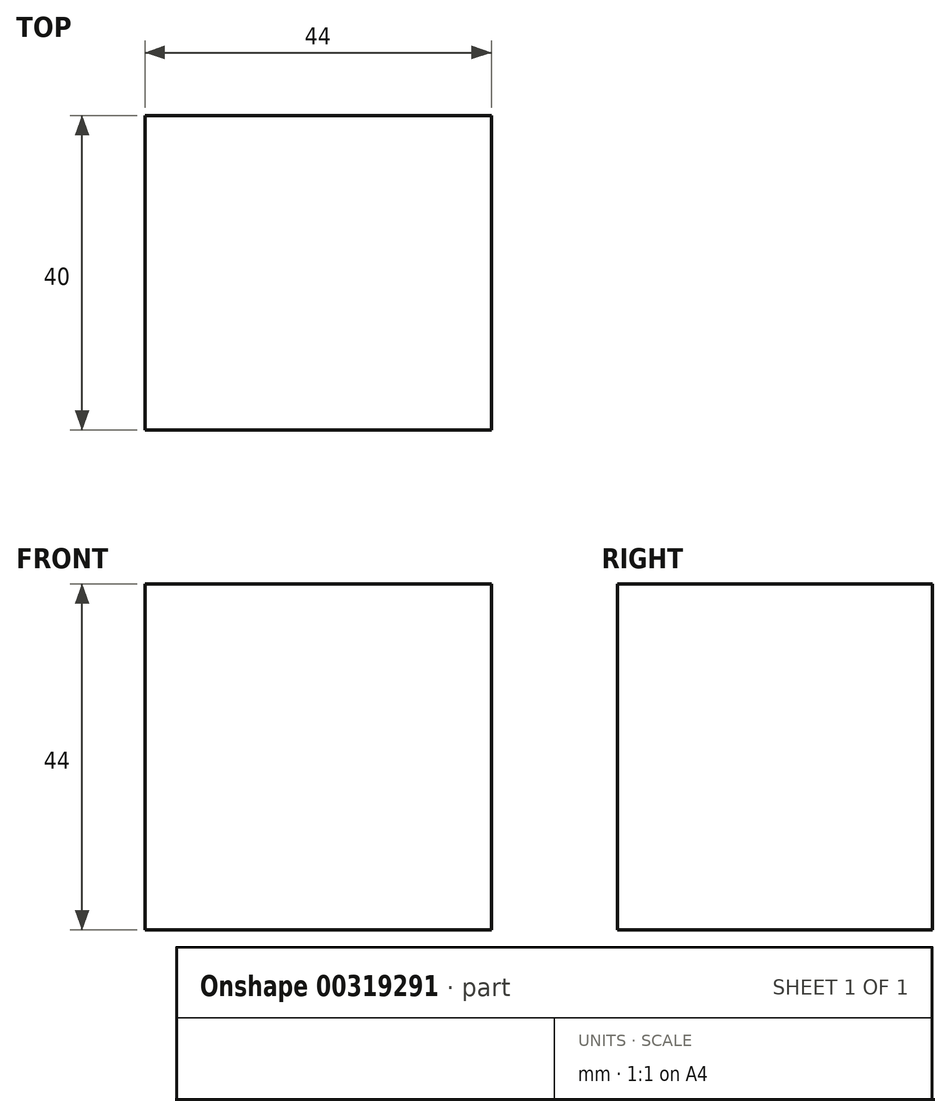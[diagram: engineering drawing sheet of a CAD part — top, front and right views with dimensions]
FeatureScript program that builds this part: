
annotation { "Feature Type Name" : "Feature", "Feature Type Description" : "" }
export const myFeature = defineFeature(function(context is Context, id is Id, definition is map)
    precondition{}
    {
        {
            var Q0;
            Q0=qCreatedBy(makeId("Front.planeOp"),FACE);
            var sketch = newSketch(context, id + "F0", { "sketchPlane" : qUnion([Q0])});
            skLineSegment(sketch, "E0.bottom", {"start": v(0, 0) * mm, "end": v(44, 0) * mm});
            skLineSegment(sketch, "E0.top", {"start": v(0, 44) * mm, "end": v(44, 44) * mm});
            skLineSegment(sketch, "E0.left", {"start": v(0, 0) * mm, "end": v(0, 44) * mm});
            skLineSegment(sketch, "E0.right", {"start": v(44, 0) * mm, "end": v(44, 44) * mm});
            skSolve(sketch);
        }
        {
            var Q0;
            Q0=makeQuery(id+"F0.imprint","IMPRINT",FACE,{"disambiguationData":[TD([[makeQuery(id+"F0.imprint","IMPRINT",EDGE,{"derivedFrom":sQuery(id+"F0.wireOp",EDGE,"E0.bottom")}),1.0]])]});
            extrude(context, id + "F1", {"entities" : qUnion([Q0]), "depth" : 40 * mm});
        }
    });
